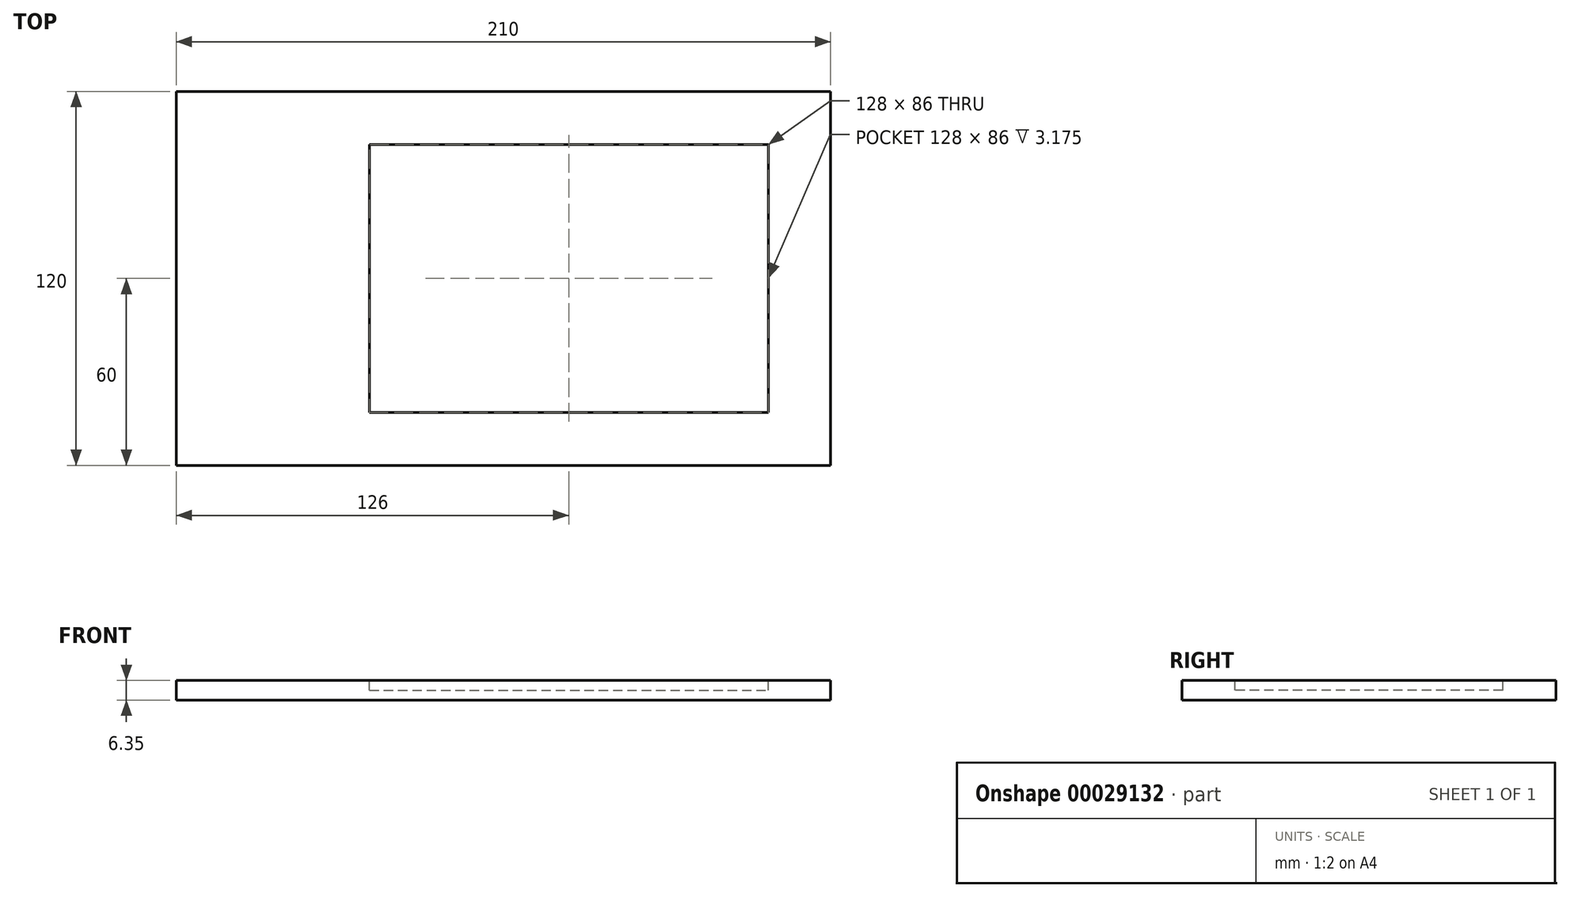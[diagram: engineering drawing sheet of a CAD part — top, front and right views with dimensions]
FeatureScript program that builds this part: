
annotation { "Feature Type Name" : "Feature", "Feature Type Description" : "" }
export const myFeature = defineFeature(function(context is Context, id is Id, definition is map)
    precondition{}
    {
        {
            var Q0;
            Q0=qCreatedBy(makeId("Top.planeOp"),FACE);
            var sketch = newSketch(context, id + "F0", { "sketchPlane" : qUnion([Q0])});
            skLineSegment(sketch, "E0.rect.bottom", {"start": v(105, -60) * mm, "end": v(-105, -60) * mm});
            skLineSegment(sketch, "E0.rect.top", {"start": v(105, 60) * mm, "end": v(-105, 60) * mm});
            skLineSegment(sketch, "E0.rect.left", {"start": v(105, -60) * mm, "end": v(105, 60) * mm});
            skLineSegment(sketch, "E0.rect.right", {"start": v(-105, -60) * mm, "end": v(-105, 60) * mm});
            skPoint(sketch, "E0.rect.middle", {"position": v(0, 0) * mm});
            skSolve(sketch);
        }
        {
            var Q0;
            Q0=makeQuery(id+"F0.imprint","IMPRINT",FACE,{"disambiguationData":[TD([[makeQuery(id+"F0.imprint","IMPRINT",EDGE,{"derivedFrom":sQuery(id+"F0.wireOp",EDGE,"E0.rect.bottom")}),-1.0]])]});
            extrude(context, id + "F1", {"entities" : qUnion([Q0]), "depth" : 6.35 * mm});
        }
        {
            var Q0;
            Q0=makeQuery(id+"F1.opExtrude","CAP_FACE",FACE,{"disambiguationData":[OSD([sQuery(id+"F0.wireOp",EDGE,"E0.rect.bottom"),sQuery(id+"F0.wireOp",EDGE,"E0.rect.top"),sQuery(id+"F0.wireOp",EDGE,"E0.rect.left"),sQuery(id+"F0.wireOp",EDGE,"E0.rect.right")])],"isStart":false});
            var sketch = newSketch(context, id + "F2", { "sketchPlane" : qUnion([Q0])});
            skLineSegment(sketch, "E1.bottom", {"start": v(-43, 43) * mm, "end": v(85, 43) * mm});
            skLineSegment(sketch, "E1.top", {"start": v(-43, -43) * mm, "end": v(85, -43) * mm});
            skLineSegment(sketch, "E1.left", {"start": v(-43, 43) * mm, "end": v(-43, -43) * mm});
            skLineSegment(sketch, "E1.right", {"start": v(85, 43) * mm, "end": v(85, -43) * mm});
            skLineSegment(sketch, "E2", {"start": v(85, 0) * mm, "end": v(105, 0) * mm, "construction": true});
            skLineSegment(sketch, "E3", {"start": v(21, -43) * mm, "end": v(21, -60) * mm, "construction": true});
            skLineSegment(sketch, "E4", {"start": v(21, 43) * mm, "end": v(21, 60) * mm, "construction": true});
            skSolve(sketch);
        }
        {
            var Q0;
            Q0 = qSketchRegion(id + "F2", true);
            extrude(context, id + "F3", {"entities" : qUnion([Q0]), "operationType" : NewBodyOperationType.REMOVE, "oppositeDirection" : true, "depth" : 3.17 * mm});
        }
    });
